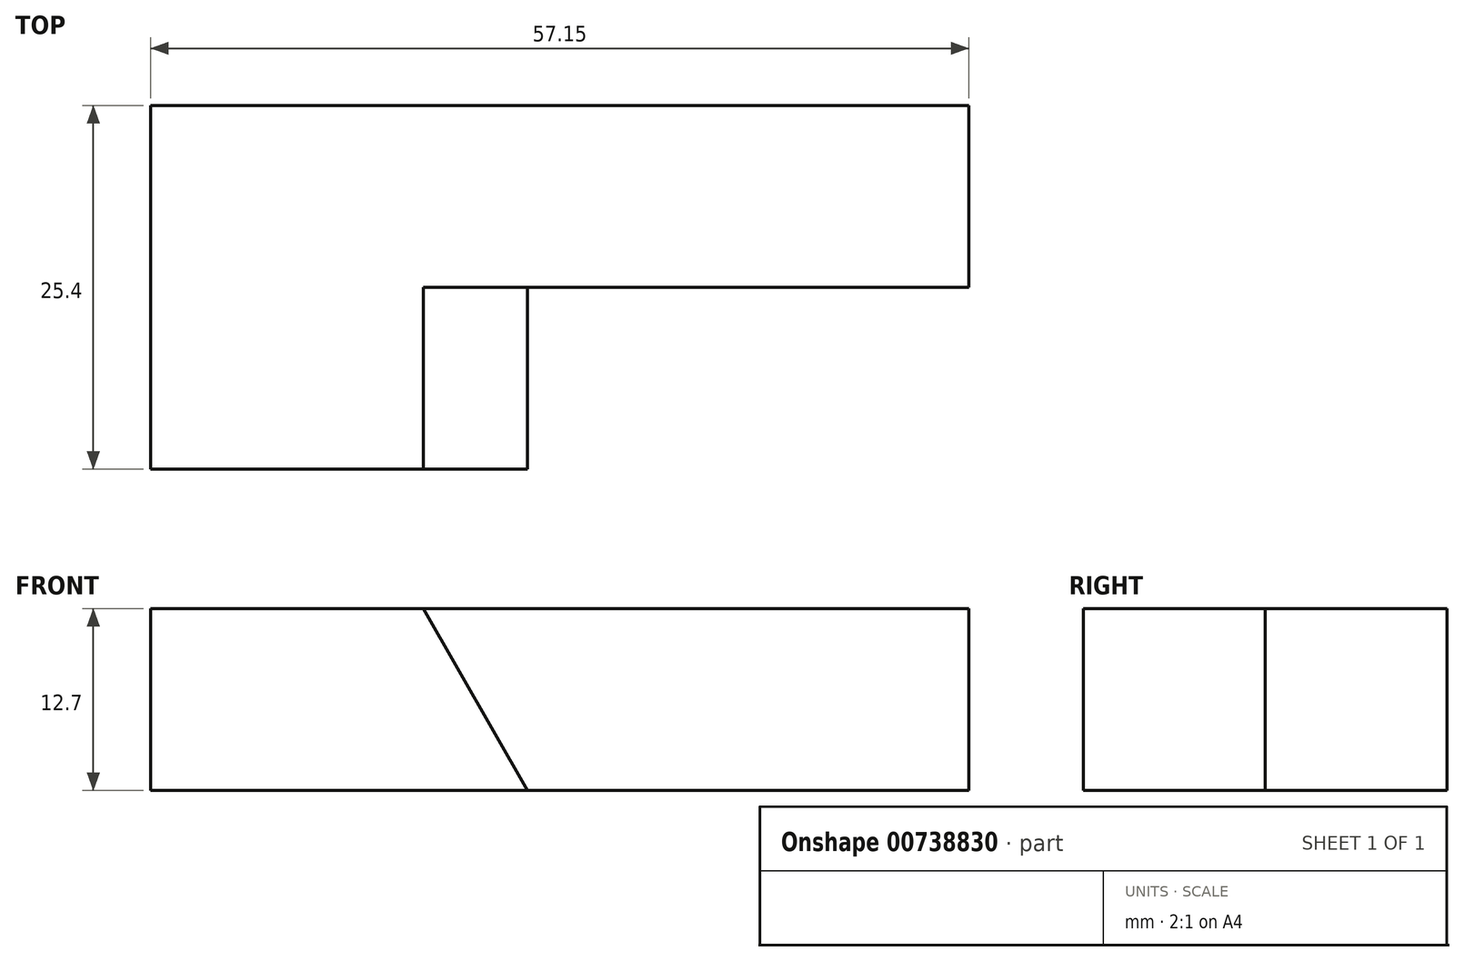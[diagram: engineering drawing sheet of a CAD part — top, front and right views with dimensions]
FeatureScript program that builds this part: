
annotation { "Feature Type Name" : "Feature", "Feature Type Description" : "" }
export const myFeature = defineFeature(function(context is Context, id is Id, definition is map)
    precondition{}
    {
        {
            var Q0;
            Q0=qCreatedBy(makeId("Front.planeOp"),FACE);
            var sketch = newSketch(context, id + "F0", { "sketchPlane" : qUnion([Q0])});
            skLineSegment(sketch, "E0", {"start": v(0, 0) * mm, "end": v(0, 44.45) * mm});
            skLineSegment(sketch, "E1", {"start": v(0, 44.45) * mm, "end": v(57.15, 44.45) * mm});
            skLineSegment(sketch, "E2", {"start": v(57.15, 44.45) * mm, "end": v(57.15, 0) * mm});
            skLineSegment(sketch, "E3", {"start": v(57.15, 0) * mm, "end": v(0, 0) * mm});
            skSolve(sketch);
        }
        {
            var Q0;
            Q0 = qSketchRegion(id + "F0", true);
            extrude(context, id + "F1", {"entities" : qUnion([Q0]), "depth" : 25.4 * mm, "offsetDistance" : 25.4 * mm});
        }
        {
            var Q0;
            Q0=makeQuery(id+"F1.opExtrude","CAP_FACE",FACE,{"disambiguationData":[OSD([sQuery(id+"F0.wireOp",EDGE,"E0"),sQuery(id+"F0.wireOp",EDGE,"E1"),sQuery(id+"F0.wireOp",EDGE,"E2"),sQuery(id+"F0.wireOp",EDGE,"E3")])],"isStart":false});
            var sketch = newSketch(context, id + "F2", { "sketchPlane" : qUnion([Q0])});
            skLineSegment(sketch, "E4", {"start": v(19.05, 44.45) * mm, "end": v(44.45, 0) * mm});
            skLineSegment(sketch, "E5", {"start": v(0, 31.75) * mm, "end": v(57.15, 31.75) * mm});
            skCircle(sketch, "E6", {"center": v(26.3, 31.75) * mm, "radius": 9.59 * mm});
            skSolve(sketch);
        }
        {
            var Q0;
            {var subQ0=sQuery(id+"F2.wireOp",EDGE,"E6");var subQ1=sQuery(id+"F2.wireOp",EDGE,"E4");var subQ2=makeQuery(id+"F2.imprint","INTERSECT",VERTEX,{"disambiguationData":[OD(0.0)],"derivedFrom":[subQ1,subQ0]});Q0=makeQuery(id+"F2.imprint","IMPRINT",FACE,{"disambiguationData":[TD([[makeQuery(id+"F2.imprint","IMPRINT",EDGE,{"disambiguationData":[TD([[subQ2,-1.0]])],"derivedFrom":subQ1}),1.0]])]});}
            var Q1;
            {var subQ0=sQuery(id+"F2.wireOp",EDGE,"E6");var subQ1=sQuery(id+"F2.wireOp",EDGE,"E4");var subQ2=makeQuery(id+"F2.imprint","INTERSECT",VERTEX,{"disambiguationData":[OD(0.0)],"derivedFrom":[subQ1,subQ0]});Q1=makeQuery(id+"F2.imprint","IMPRINT",FACE,{"disambiguationData":[TD([[makeQuery(id+"F2.imprint","IMPRINT",EDGE,{"disambiguationData":[TD([[subQ2,-1.0]])],"derivedFrom":subQ1}),-1.0]])]});}
            var Q2;
            {var subQ0=sQuery(id+"F2.wireOp",EDGE,"E5");var subQ1=sQuery(id+"F2.wireOp",EDGE,"E4");var subQ2=makeQuery(id+"F2.imprint","INTERSECT",VERTEX,{"derivedFrom":[subQ1,subQ0]});Q2=makeQuery(id+"F2.imprint","IMPRINT",FACE,{"disambiguationData":[TD([[makeQuery(id+"F2.imprint","IMPRINT",EDGE,{"disambiguationData":[TD([[subQ2,-1.0]])],"derivedFrom":subQ1}),-1.0]])]});}
            var Q3;
            {var subQ0=sQuery(id+"F2.wireOp",EDGE,"E5");var subQ1=sQuery(id+"F2.wireOp",EDGE,"E4");var subQ2=makeQuery(id+"F2.imprint","INTERSECT",VERTEX,{"derivedFrom":[subQ1,subQ0]});Q3=makeQuery(id+"F2.imprint","IMPRINT",FACE,{"disambiguationData":[TD([[makeQuery(id+"F2.imprint","IMPRINT",EDGE,{"disambiguationData":[TD([[subQ2,-1.0]])],"derivedFrom":subQ1}),1.0]])]});}
            extrude(context, id + "F3", {"entities" : qUnion([Q0, Q1, Q2, Q3]), "operationType" : NewBodyOperationType.REMOVE, "endBound" : BoundingType.THROUGH_ALL, "oppositeDirection" : true, "depth" : 25.4 * mm, "offsetDistance" : 25.4 * mm});
        }
        {
            var Q0;
            Q0=makeQuery(id+"F1.opExtrude","CAP_FACE",FACE,{"disambiguationData":[OSD([sQuery(id+"F0.wireOp",EDGE,"E0"),sQuery(id+"F0.wireOp",EDGE,"E1"),sQuery(id+"F0.wireOp",EDGE,"E2"),sQuery(id+"F0.wireOp",EDGE,"E3")])],"isStart":false});
            var sketch = newSketch(context, id + "F4", { "sketchPlane" : qUnion([Q0])});
            skLineSegment(sketch, "E7", {"start": v(19.05, 44.45) * mm, "end": v(44.45, 0) * mm});
            skSolve(sketch);
        }
        {
            var Q0;
            {var subQ0=makeQuery(id+"F1.opExtrude","CAP_EDGE",EDGE,{"disambiguationData":[OSD([sQuery(id+"F0.wireOp",EDGE,"E2")])],"isStart":false});Q0=makeQuery(id+"F4.imprint","IMPRINT",FACE,{"disambiguationData":[TD([[makeQuery(id+"F4.imprint","IMPRINT",EDGE,{"derivedFrom":subQ0}),-1.0]])]});}
            extrude(context, id + "F5", {"entities" : qUnion([Q0]), "operationType" : NewBodyOperationType.REMOVE, "oppositeDirection" : true, "depth" : 12.7 * mm, "offsetDistance" : 25.4 * mm});
        }
    });
